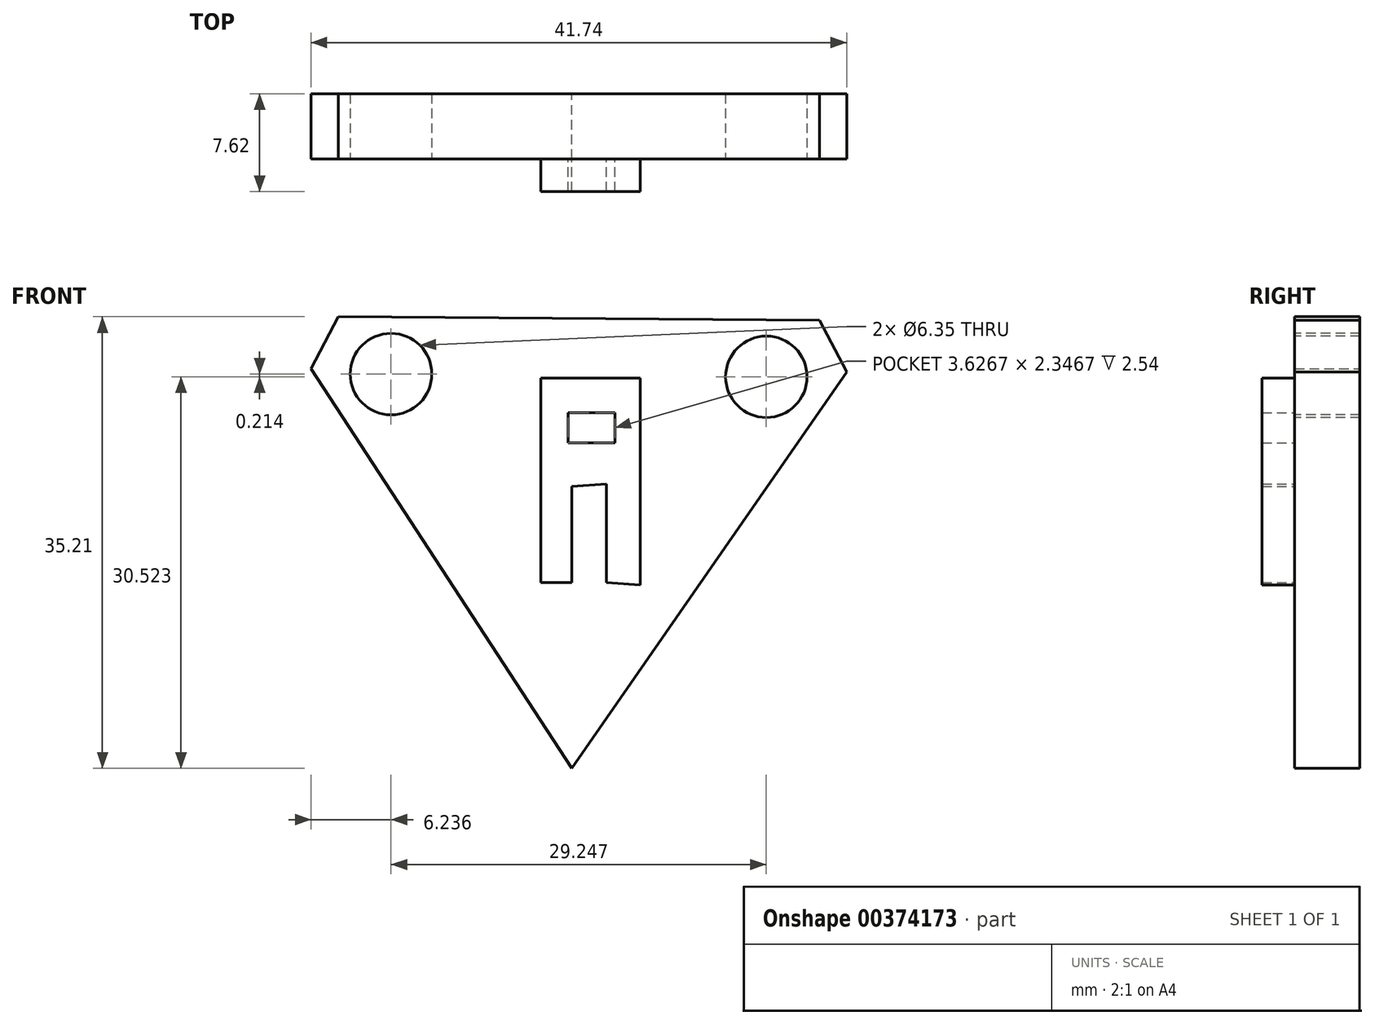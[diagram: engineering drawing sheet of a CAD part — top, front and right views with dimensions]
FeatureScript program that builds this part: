
annotation { "Feature Type Name" : "Feature", "Feature Type Description" : "" }
export const myFeature = defineFeature(function(context is Context, id is Id, definition is map)
    precondition{}
    {
        {
            var Q0;
            Q0=qCreatedBy(makeId("Front.planeOp"),FACE);
            var sketch = newSketch(context, id + "F0", { "sketchPlane" : qUnion([Q0])});
            skLineSegment(sketch, "E0", {"start": v(-29.3, 43.85) * mm, "end": v(-9, 12.68) * mm});
            skLineSegment(sketch, "E1", {"start": v(-9, 12.68) * mm, "end": v(12.43, 43.57) * mm});
            skLineSegment(sketch, "E2", {"start": v(-29.3, 43.85) * mm, "end": v(-27.18, 47.9) * mm});
            skLineSegment(sketch, "E3", {"start": v(12.43, 43.57) * mm, "end": v(10.31, 47.62) * mm});
            skLineSegment(sketch, "E4", {"start": v(-27.18, 47.9) * mm, "end": v(10.31, 47.62) * mm});
            skSolve(sketch);
        }
        {
            var Q0;
            Q0=makeQuery(id+"F0.imprint","IMPRINT",FACE,{"disambiguationData":[TD([[makeQuery(id+"F0.imprint","IMPRINT",EDGE,{"derivedFrom":sQuery(id+"F0.wireOp",EDGE,"E0")}),1.0]])]});
            extrude(context, id + "F1", {"entities" : qUnion([Q0]), "depth" : 5.08 * mm});
        }
        {
            var Q0;
            Q0=makeQuery(id+"F1.opExtrude","CAP_FACE",FACE,{"disambiguationData":[OSD([sQuery(id+"F0.wireOp",EDGE,"E0"),sQuery(id+"F0.wireOp",EDGE,"E1"),sQuery(id+"F0.wireOp",EDGE,"E2"),sQuery(id+"F0.wireOp",EDGE,"E3"),sQuery(id+"F0.wireOp",EDGE,"E4")])],"isStart":false});
            var sketch = newSketch(context, id + "F2", { "sketchPlane" : qUnion([Q0])});
            skCircle(sketch, "E5", {"center": v(6.17, 43.2) * mm, "radius": 3.18 * mm});
            skCircle(sketch, "E6", {"center": v(-23.07, 43.42) * mm, "radius": 3.18 * mm});
            skSolve(sketch);
        }
        {
            var Q0;
            Q0=makeQuery(id+"F2.imprint","IMPRINT",FACE,{"disambiguationData":[TD([[makeQuery(id+"F2.imprint","IMPRINT",EDGE,{"derivedFrom":sQuery(id+"F2.wireOp",EDGE,"E5")}),1.0]])]});
            var Q1;
            Q1=makeQuery(id+"F2.imprint","IMPRINT",FACE,{"disambiguationData":[TD([[makeQuery(id+"F2.imprint","IMPRINT",EDGE,{"derivedFrom":sQuery(id+"F2.wireOp",EDGE,"E6")}),1.0]])]});
            extrude(context, id + "F3", {"entities" : qUnion([Q0, Q1]), "operationType" : NewBodyOperationType.REMOVE, "endBound" : BoundingType.THROUGH_ALL, "oppositeDirection" : true, "depth" : 25.4 * mm});
        }
        {
            var Q0;
            Q0=makeQuery(id+"F1.opExtrude","CAP_FACE",FACE,{"disambiguationData":[OSD([sQuery(id+"F0.wireOp",EDGE,"E0"),sQuery(id+"F0.wireOp",EDGE,"E1"),sQuery(id+"F0.wireOp",EDGE,"E2"),sQuery(id+"F0.wireOp",EDGE,"E3"),sQuery(id+"F0.wireOp",EDGE,"E4")])],"isStart":false});
            var sketch = newSketch(context, id + "F4", { "sketchPlane" : qUnion([Q0])});
            skLineSegment(sketch, "E7", {"start": v(-11.4, 43.1) * mm, "end": v(-3.67, 43.1) * mm});
            skLineSegment(sketch, "E8", {"start": v(-11.4, 43.1) * mm, "end": v(-11.4, 27.18) * mm});
            skLineSegment(sketch, "E9", {"start": v(-11.4, 27.18) * mm, "end": v(-9, 27.18) * mm});
            skLineSegment(sketch, "E10", {"start": v(-9, 27.18) * mm, "end": v(-9, 34.64) * mm});
            skLineSegment(sketch, "E11", {"start": v(-9, 34.64) * mm, "end": v(-6.3, 34.85) * mm});
            skLineSegment(sketch, "E12", {"start": v(-6.3, 34.85) * mm, "end": v(-6.3, 27.18) * mm});
            skLineSegment(sketch, "E13", {"start": v(-3.67, 43.1) * mm, "end": v(-3.67, 26.96) * mm});
            skLineSegment(sketch, "E14", {"start": v(-3.67, 26.96) * mm, "end": v(-6.3, 27.18) * mm});
            skLineSegment(sketch, "E15.bottom", {"start": v(-9.26, 40.4) * mm, "end": v(-5.63, 40.4) * mm});
            skLineSegment(sketch, "E15.top", {"start": v(-9.26, 38.06) * mm, "end": v(-5.63, 38.06) * mm});
            skLineSegment(sketch, "E15.left", {"start": v(-9.26, 40.4) * mm, "end": v(-9.26, 38.06) * mm});
            skLineSegment(sketch, "E15.right", {"start": v(-5.63, 40.4) * mm, "end": v(-5.63, 38.06) * mm});
            skSolve(sketch);
        }
        {
            var Q0;
            Q0=makeQuery(id+"F4.imprint","IMPRINT",FACE,{"disambiguationData":[TD([[makeQuery(id+"F4.imprint","IMPRINT",EDGE,{"derivedFrom":sQuery(id+"F4.wireOp",EDGE,"E7")}),-1.0]])]});
            extrude(context, id + "F5", {"entities" : qUnion([Q0]), "operationType" : NewBodyOperationType.ADD, "depth" : 2.54 * mm});
        }
    });
